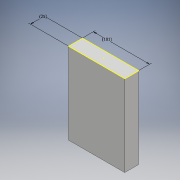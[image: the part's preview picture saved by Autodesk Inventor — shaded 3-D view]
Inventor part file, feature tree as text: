
AUTODESK INVENTOR PART (.ipt)
format: ipt  version: 2017 (Build 210142000, 142)  size: 97,792 bytes
history: native  units: mm
features: sketch x2, extrude x1, projected_geometry x1
ambient origin geometry x8: Origin, YZ Plane, XZ Plane, XY Plane, X Axis, Y Axis, Z Axis, Center Point
bodies: Solid1 (feature_tree)
feature tree (4):
  extrude  "Extrusion1"  Depth=25.0mm
  sketch  "Sketch2"  dims[d2=146.0mm d3=0.0mm d4=101.0mm d5=25.0mm]
  sketch  "Sketch1"  dims[d0=101.0mm d1=25.0mm]
  projected_geometry  "Projected Loop1"
